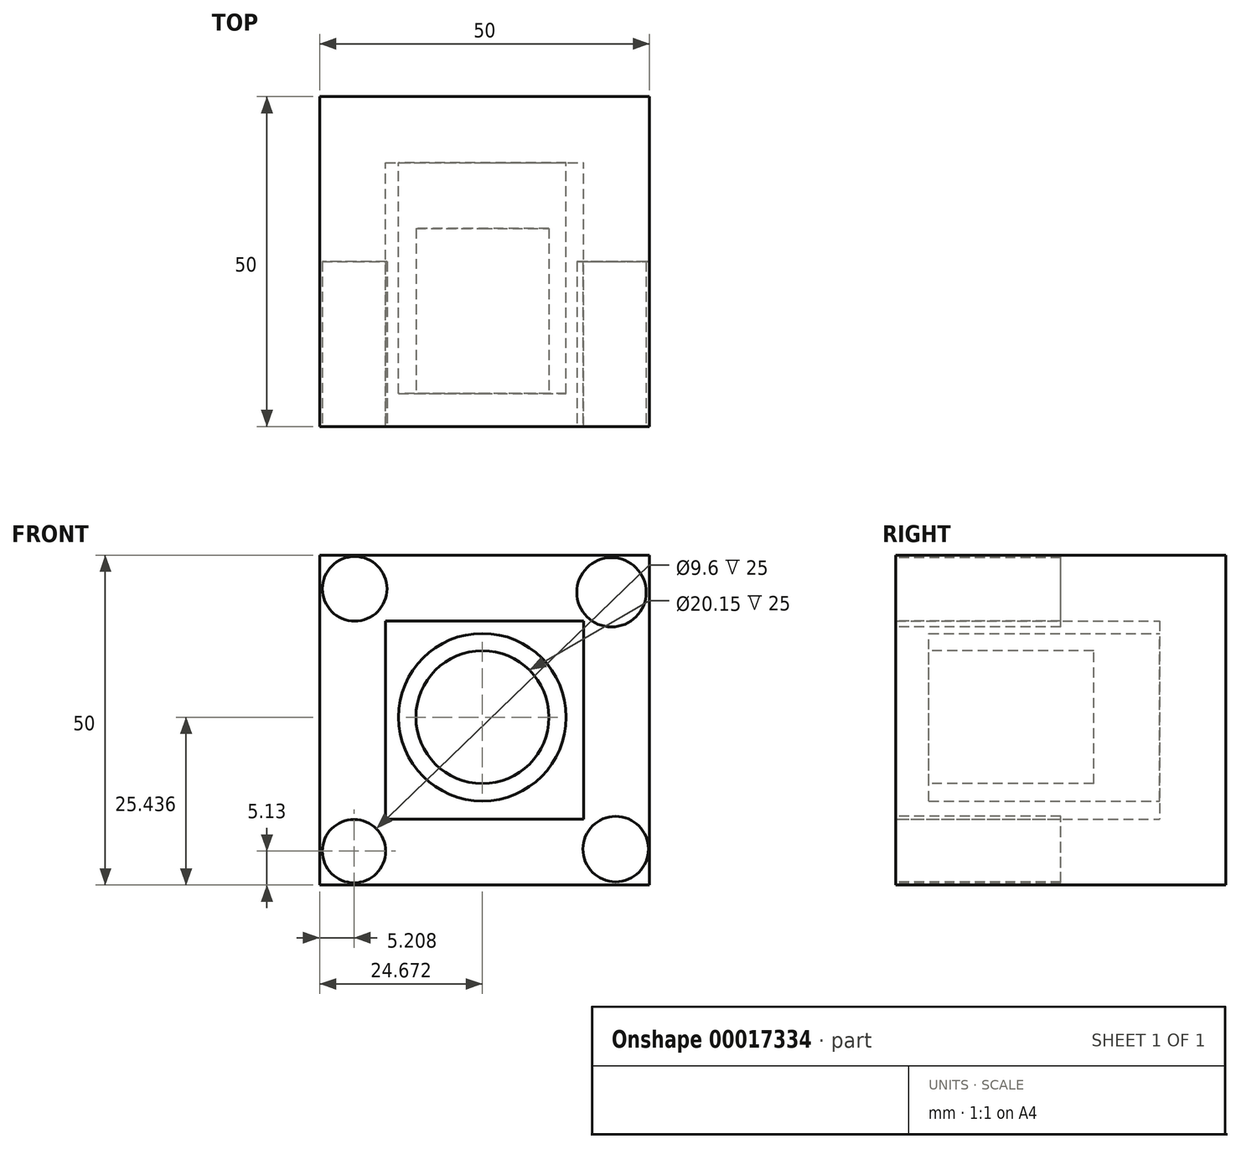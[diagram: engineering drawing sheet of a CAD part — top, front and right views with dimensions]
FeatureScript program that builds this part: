
annotation { "Feature Type Name" : "Feature", "Feature Type Description" : "" }
export const myFeature = defineFeature(function(context is Context, id is Id, definition is map)
    precondition{}
    {
        {
            var Q0;
            Q0=qCreatedBy(makeId("Front.planeOp"),FACE);
            var sketch = newSketch(context, id + "F0", { "sketchPlane" : qUnion([Q0])});
            skLineSegment(sketch, "E0.bottom", {"start": v(-19.74, 28.1) * mm, "end": v(30.26, 28.1) * mm});
            skLineSegment(sketch, "E0.top", {"start": v(-19.74, -21.9) * mm, "end": v(30.26, -21.9) * mm});
            skLineSegment(sketch, "E0.left", {"start": v(-19.74, 28.1) * mm, "end": v(-19.74, -21.9) * mm});
            skLineSegment(sketch, "E0.right", {"start": v(30.26, 28.1) * mm, "end": v(30.26, -21.9) * mm});
            skSolve(sketch);
        }
        {
            var Q0;
            Q0=makeQuery(id+"F0.imprint","IMPRINT",FACE,{"disambiguationData":[TD([[makeQuery(id+"F0.imprint","IMPRINT",EDGE,{"derivedFrom":sQuery(id+"F0.wireOp",EDGE,"E0.bottom")}),-1.0]])]});
            extrude(context, id + "F1", {"entities" : qUnion([Q0]), "depth" : 50 * mm});
        }
        {
            var Q0;
            Q0=makeQuery(id+"F1.opExtrude","CAP_FACE",FACE,{"disambiguationData":[OSD([sQuery(id+"F0.wireOp",EDGE,"E0.bottom"),sQuery(id+"F0.wireOp",EDGE,"E0.top"),sQuery(id+"F0.wireOp",EDGE,"E0.left"),sQuery(id+"F0.wireOp",EDGE,"E0.right")])],"isStart":false});
            shell(context, id + "F2", {"entities" : qUnion([Q0]), "thickness" : 10 * mm});
        }
        {
            var Q0;
            Q0=makeQuery(id+"F2.opShell","OFFSET_FACE",FACE,{"disambiguationData":[OSD([sQuery(id+"F0.wireOp",EDGE,"E0.bottom"),sQuery(id+"F0.wireOp",EDGE,"E0.top"),sQuery(id+"F0.wireOp",EDGE,"E0.left"),sQuery(id+"F0.wireOp",EDGE,"E0.right")])]});
            var sketch = newSketch(context, id + "F3", { "sketchPlane" : qUnion([Q0])});
            skCircle(sketch, "E1", {"center": v(4.93, 3.55) * mm, "radius": 12.7 * mm});
            skSolve(sketch);
        }
        {
            var Q0;
            Q0=makeQuery(id+"F3.imprint","IMPRINT",FACE,{"disambiguationData":[TD([[makeQuery(id+"F3.imprint","IMPRINT",EDGE,{"derivedFrom":sQuery(id+"F3.wireOp",EDGE,"E1")}),1.0]])]});
            extrude(context, id + "F4", {"entities" : qUnion([Q0]), "operationType" : NewBodyOperationType.ADD, "depth" : 35 * mm});
        }
        {
            var Q0;
            Q0=makeQuery(id+"F1.opExtrude","CAP_FACE",FACE,{"disambiguationData":[OSD([sQuery(id+"F0.wireOp",EDGE,"E0.bottom"),sQuery(id+"F0.wireOp",EDGE,"E0.top"),sQuery(id+"F0.wireOp",EDGE,"E0.left"),sQuery(id+"F0.wireOp",EDGE,"E0.right")])],"isStart":false});
            var sketch = newSketch(context, id + "F5", { "sketchPlane" : qUnion([Q0])});
            skCircle(sketch, "E2", {"center": v(-14.43, 23) * mm, "radius": 4.9 * mm});
            skCircle(sketch, "E3", {"center": v(24.5, 22.48) * mm, "radius": 5.25 * mm});
            skCircle(sketch, "E4", {"center": v(-14.53, -16.76) * mm, "radius": 4.8 * mm});
            skCircle(sketch, "E5", {"center": v(25.13, -16.44) * mm, "radius": 4.97 * mm});
            skSolve(sketch);
        }
        {
            var Q0;
            Q0=makeQuery(id+"F5.imprint","IMPRINT",FACE,{"disambiguationData":[TD([[makeQuery(id+"F5.imprint","IMPRINT",EDGE,{"derivedFrom":sQuery(id+"F5.wireOp",EDGE,"E2")}),1.0]])]});
            var Q1;
            Q1=makeQuery(id+"F5.imprint","IMPRINT",FACE,{"disambiguationData":[TD([[makeQuery(id+"F5.imprint","IMPRINT",EDGE,{"derivedFrom":sQuery(id+"F5.wireOp",EDGE,"E3")}),1.0]])]});
            var Q2;
            Q2=makeQuery(id+"F5.imprint","IMPRINT",FACE,{"disambiguationData":[TD([[makeQuery(id+"F5.imprint","IMPRINT",EDGE,{"derivedFrom":sQuery(id+"F5.wireOp",EDGE,"E5")}),1.0]])]});
            var Q3;
            Q3=makeQuery(id+"F5.imprint","IMPRINT",FACE,{"disambiguationData":[TD([[makeQuery(id+"F5.imprint","IMPRINT",EDGE,{"derivedFrom":sQuery(id+"F5.wireOp",EDGE,"E4")}),1.0]])]});
            extrude(context, id + "F6", {"entities" : qUnion([Q0, Q1, Q2, Q3]), "operationType" : NewBodyOperationType.REMOVE, "oppositeDirection" : true, "depth" : 25 * mm});
        }
        {
            var Q0;
            Q0=makeQuery(id+"F4.opExtrude","CAP_FACE",FACE,{"disambiguationData":[OSD([sQuery(id+"F3.wireOp",EDGE,"E1")])],"isStart":false});
            var sketch = newSketch(context, id + "F7", { "sketchPlane" : qUnion([Q0])});
            skCircle(sketch, "E6", {"center": v(4.93, 3.55) * mm, "radius": 10.08 * mm});
            skSolve(sketch);
        }
        {
            var Q0;
            Q0=makeQuery(id+"F7.imprint","IMPRINT",FACE,{"disambiguationData":[TD([[makeQuery(id+"F7.imprint","IMPRINT",EDGE,{"derivedFrom":sQuery(id+"F7.wireOp",EDGE,"E6")}),1.0]])]});
            extrude(context, id + "F8", {"entities" : qUnion([Q0]), "operationType" : NewBodyOperationType.REMOVE, "oppositeDirection" : true, "depth" : 25 * mm});
        }
    });
